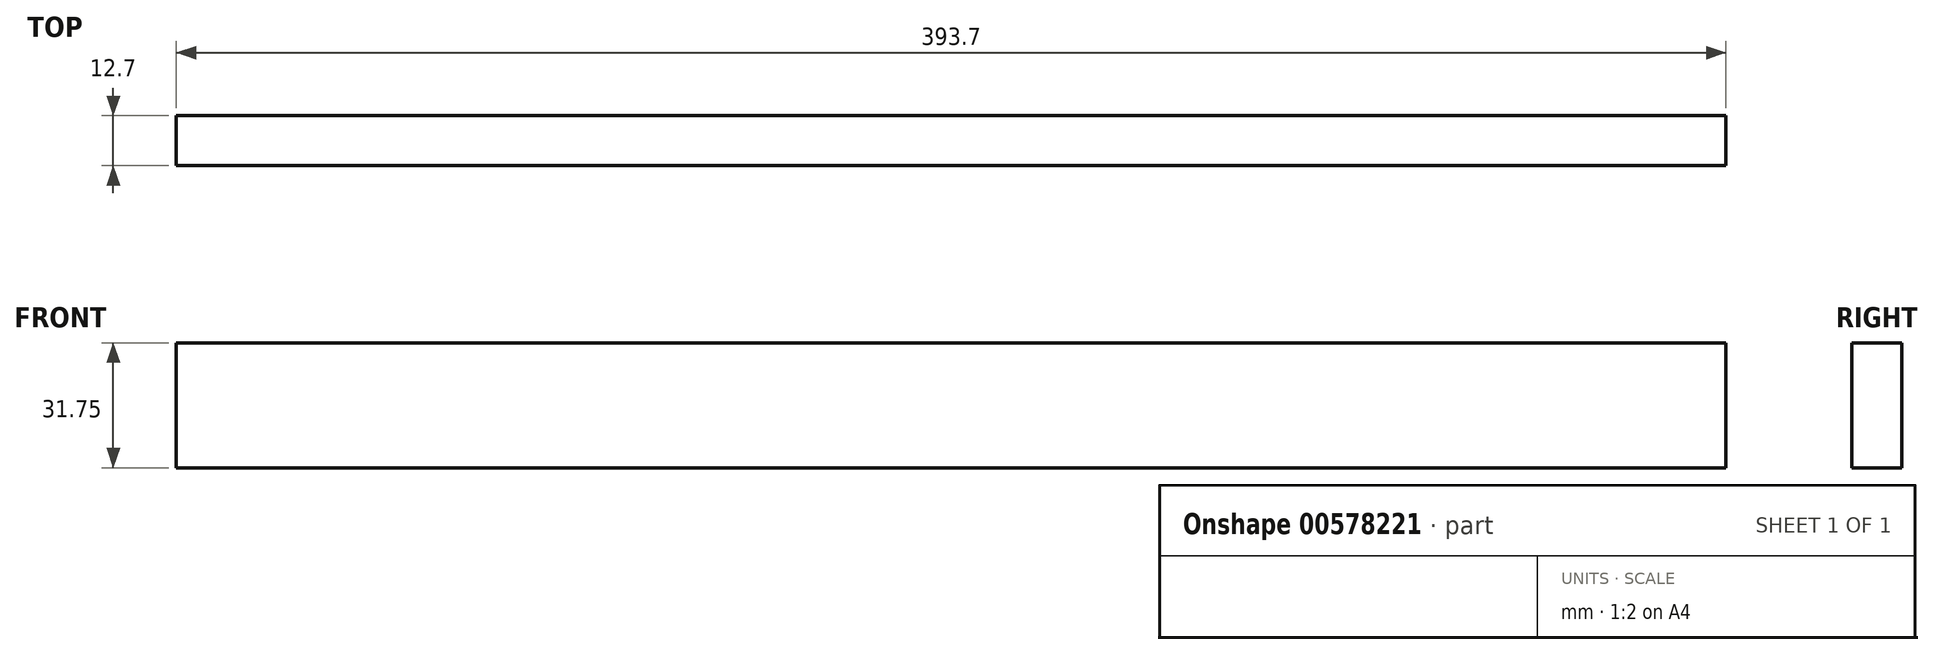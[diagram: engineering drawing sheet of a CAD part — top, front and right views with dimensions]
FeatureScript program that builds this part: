
annotation { "Feature Type Name" : "Feature", "Feature Type Description" : "" }
export const myFeature = defineFeature(function(context is Context, id is Id, definition is map)
    precondition{}
    {
        {
            var Q0;
            Q0=qCreatedBy(makeId("Front.planeOp"),FACE);
            var sketch = newSketch(context, id + "F0", { "sketchPlane" : qUnion([Q0])});
            skLineSegment(sketch, "E0.bottom", {"start": v(-184.95, -18.22) * mm, "end": v(208.75, -18.22) * mm});
            skLineSegment(sketch, "E0.top", {"start": v(-184.95, -49.97) * mm, "end": v(208.75, -49.97) * mm});
            skLineSegment(sketch, "E0.left", {"start": v(-184.95, -18.22) * mm, "end": v(-184.95, -49.97) * mm});
            skLineSegment(sketch, "E0.right", {"start": v(208.75, -18.22) * mm, "end": v(208.75, -49.97) * mm});
            skSolve(sketch);
        }
        {
            var Q0;
            Q0 = qSketchRegion(id + "F0", true);
            extrude(context, id + "F1", {"entities" : qUnion([Q0]), "depth" : 12.7 * mm, "offsetDistance" : 25.4 * mm});
        }
    });
